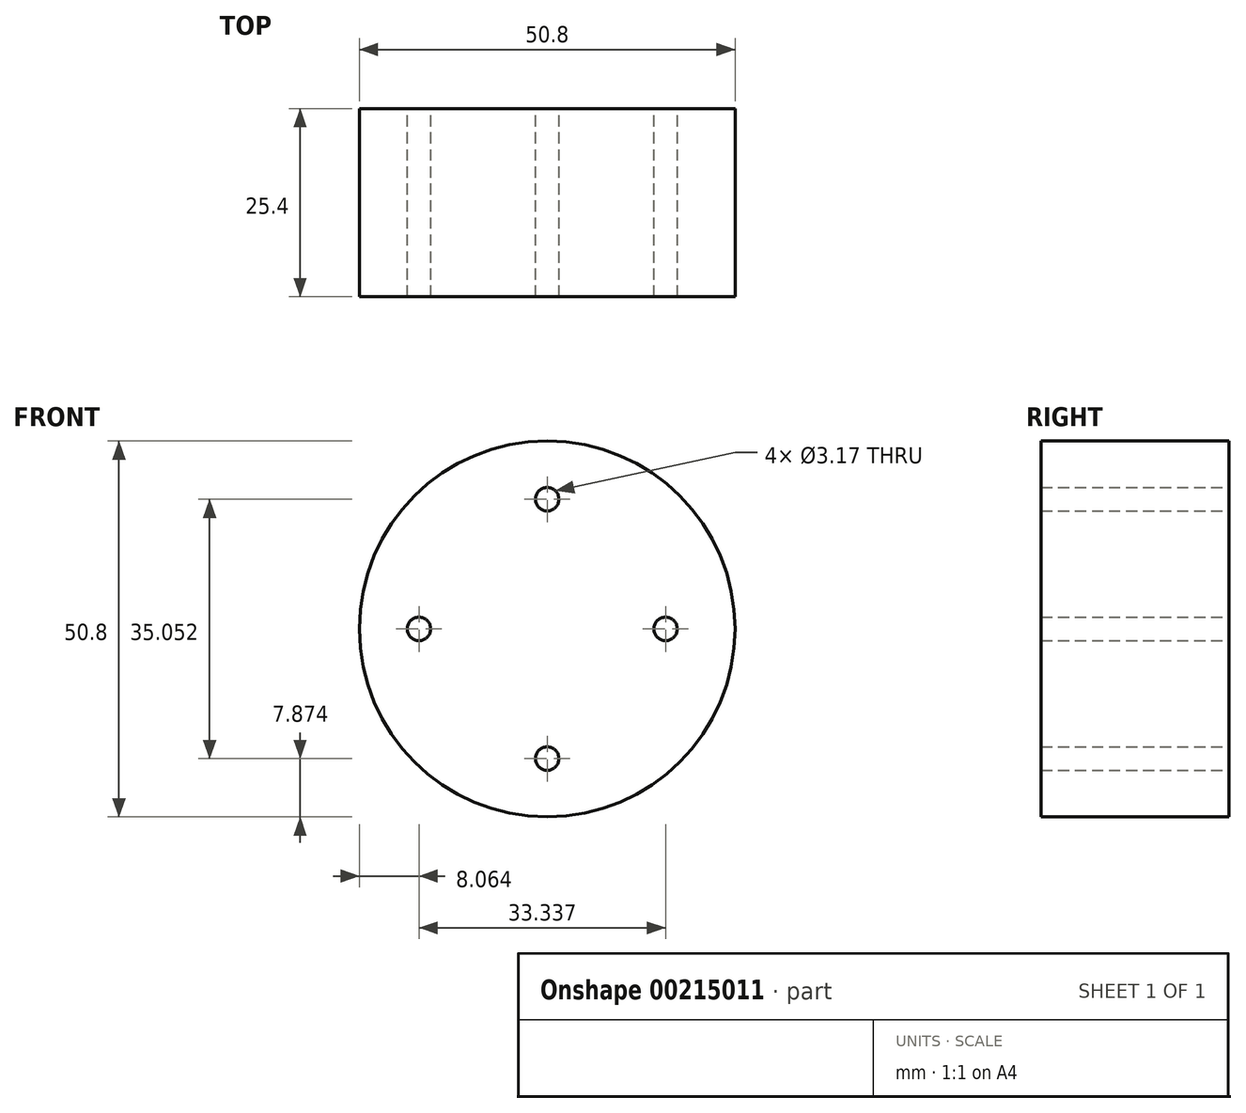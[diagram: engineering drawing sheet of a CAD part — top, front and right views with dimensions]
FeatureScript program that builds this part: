
annotation { "Feature Type Name" : "Feature", "Feature Type Description" : "" }
export const myFeature = defineFeature(function(context is Context, id is Id, definition is map)
    precondition{}
    {
        {
            var Q0;
            Q0=qCreatedBy(makeId("Front.planeOp"),FACE);
            var sketch = newSketch(context, id + "F0", { "sketchPlane" : qUnion([Q0])});
            skCircle(sketch, "E0", {"center": v(0, 0) * mm, "radius": 25.4 * mm});
            skCircle(sketch, "E1", {"center": v(0, 0) * mm, "radius": 22.23 * mm});
            skSolve(sketch);
        }
        {
            var Q0;
            Q0=makeQuery(id+"F0.imprint","IMPRINT",FACE,{"disambiguationData":[TD([[makeQuery(id+"F0.imprint","IMPRINT",EDGE,{"derivedFrom":sQuery(id+"F0.wireOp",EDGE,"E1")}),1.0]])]});
            var sketch = newSketch(context, id + "F1", { "sketchPlane" : qUnion([Q0])});
            skCircle(sketch, "E2", {"center": v(0, 17.53) * mm, "radius": 1.59 * mm});
            skCircle(sketch, "E3", {"center": v(0, -17.53) * mm, "radius": 1.59 * mm});
            skCircle(sketch, "E4", {"center": v(16, 0) * mm, "radius": 1.59 * mm});
            skCircle(sketch, "E5", {"center": v(-17.34, 0) * mm, "radius": 1.59 * mm});
            skSolve(sketch);
        }
        {
            var Q0;
            Q0=makeQuery(id+"F0.imprint","IMPRINT",FACE,{"disambiguationData":[TD([[makeQuery(id+"F0.imprint","IMPRINT",EDGE,{"derivedFrom":sQuery(id+"F0.wireOp",EDGE,"E0")}),1.0]])]});
            var Q1;
            Q1=makeQuery(id+"F0.imprint","IMPRINT",FACE,{"disambiguationData":[TD([[makeQuery(id+"F0.imprint","IMPRINT",EDGE,{"derivedFrom":sQuery(id+"F0.wireOp",EDGE,"E1")}),1.0]])]});
            extrude(context, id + "F2", {"entities" : qUnion([Q0, Q1]), "depth" : 25.4 * mm});
        }
        {
            var Q0;
            Q0=sQuery(id+"F1.wireOp",VERTEX,"E2.center");
            var Q1;
            Q1=sQuery(id+"F1.wireOp",VERTEX,"E4.center");
            var Q2;
            Q2=sQuery(id+"F1.wireOp",VERTEX,"E3.center");
            var Q3;
            Q3=sQuery(id+"F1.wireOp",VERTEX,"E5.center");
            var Q4;
            Q4=makeQuery(id+"F2.opExtrude","SWEPT_BODY",BODY,{"disambiguationData":[OSD([sQuery(id+"F0.wireOp",EDGE,"E0")])]});
            hole(context, id + "F3", {"style" : HoleStyle.SIMPLE, "endStyle" : HoleEndStyle.THROUGH, "oppositeDirection" : true, "holeDiameter" : 3.17 * mm, "isTappedThrough" : true, "tappedDepth" : 12.7 * mm, "tapClearance" : 3, "locations" : qUnion([Q0, Q1, Q2, Q3]), "scope" : qUnion([Q4])});
        }
    });
